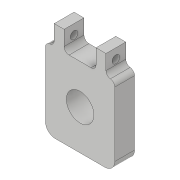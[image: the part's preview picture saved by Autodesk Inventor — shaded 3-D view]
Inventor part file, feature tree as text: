
AUTODESK INVENTOR PART (.ipt)
format: ipt  version: 2018.3 (Build 223284000, 284)  size: 138,240 bytes
history: native  units: in
note: dims shown in document units (in); Inventor stores cm internally (conversion verified against a paired STEP export)
features: extrude x3, sketch x3, fillet x2
ambient origin geometry x8: Origin, YZ Plane, XZ Plane, XY Plane, X Axis, Y Axis, Z Axis, Center Point
bodies: Solid1 (feature_tree)
feature tree (8):
  extrude  "Extrusion1"  Depth=2.0in
  extrude  "Extrusion2"  Depth=0.222in
  extrude  "Extrusion3"  Depth=0.25in
  fillet  "Fillet2"  Radius=0.806in
  fillet  "Fillet3"  Radius=0.5in
  sketch  "Sketch1"  dims[d0=1.75in d1=2.0in]
  sketch  "Sketch2"  dims[d2=0.222in d3=0.222in]
  sketch  "Sketch3"  dims[d4=0.25in d5=0.25in d6=0.806in d7=0.5in d8=0.0in d9=0.755in d10=0.695in d11=0.5in d12=0.0in d13=0.1925in d14=0.25in d15=0.25in d16=0.5in d17=0.0in d19=0.25in d20=0.5in d21=0.875in d22=1.0in d23=0.875in d24=0.125in]
